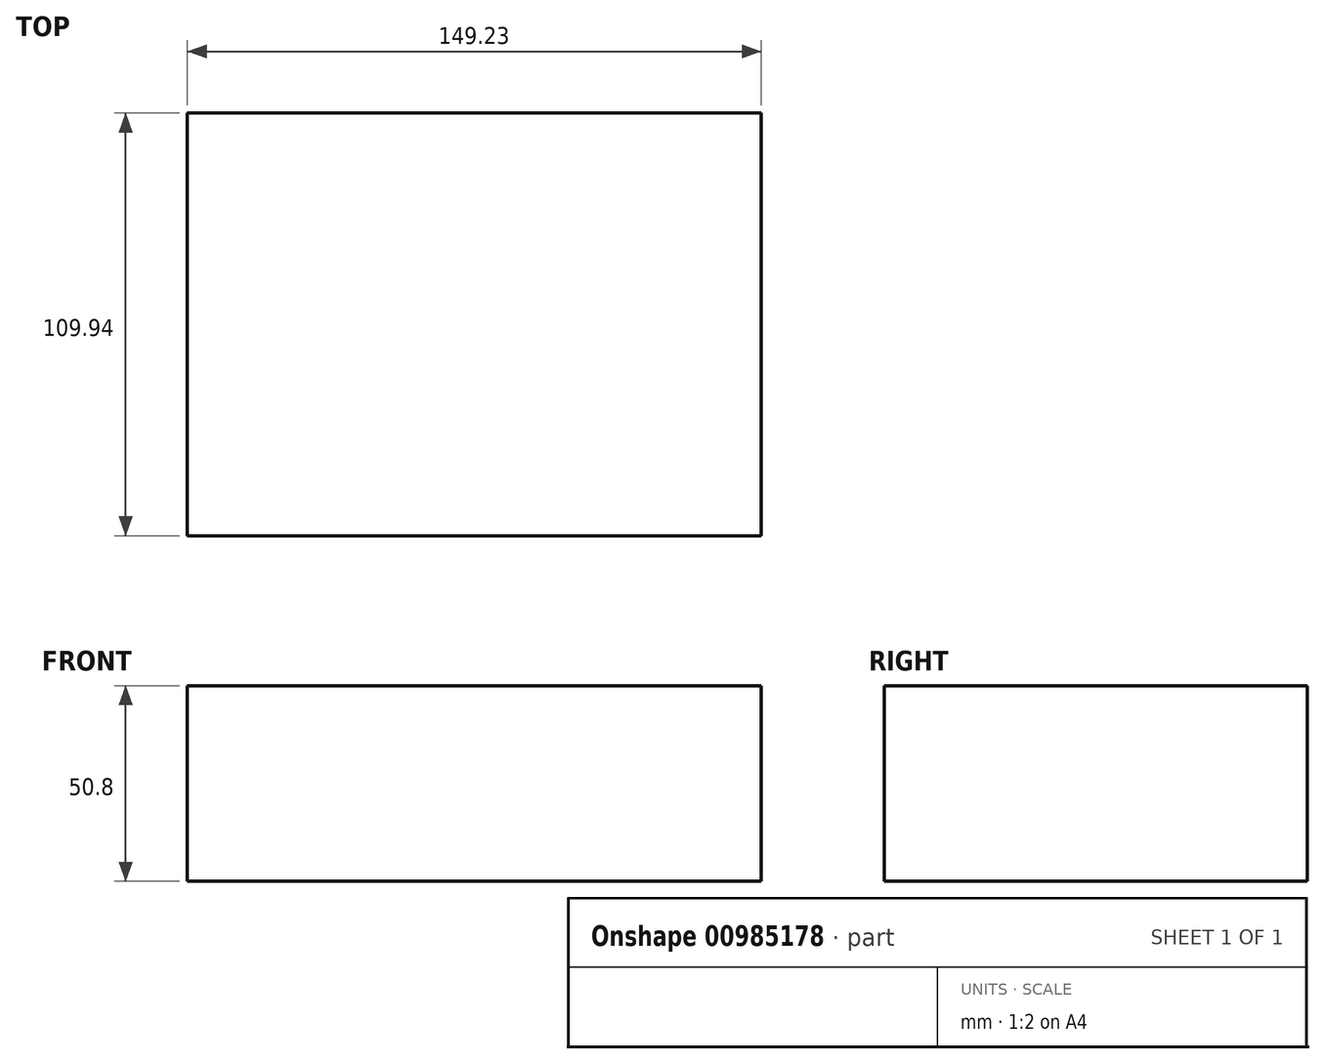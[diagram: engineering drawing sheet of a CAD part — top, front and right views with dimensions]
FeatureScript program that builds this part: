
annotation { "Feature Type Name" : "Feature", "Feature Type Description" : "" }
export const myFeature = defineFeature(function(context is Context, id is Id, definition is map)
    precondition{}
    {
        {
            var Q0;
            Q0=qCreatedBy(makeId("Top.planeOp"),FACE);
            var sketch = newSketch(context, id + "F0", { "sketchPlane" : qUnion([Q0])});
            skLineSegment(sketch, "E0.bottom", {"start": v(-73.38, 44.02) * mm, "end": v(75.85, 44.02) * mm});
            skLineSegment(sketch, "E0.top", {"start": v(-73.38, -65.92) * mm, "end": v(75.85, -65.92) * mm});
            skLineSegment(sketch, "E0.left", {"start": v(-73.38, 44.02) * mm, "end": v(-73.38, -65.92) * mm});
            skLineSegment(sketch, "E0.right", {"start": v(75.85, 44.02) * mm, "end": v(75.85, -65.92) * mm});
            skSolve(sketch);
        }
        {
            var Q0;
            Q0 = qSketchRegion(id + "F0", true);
            extrude(context, id + "F1", {"entities" : qUnion([Q0]), "depth" : 50.8 * mm, "offsetDistance" : 25.4 * mm});
        }
    });
